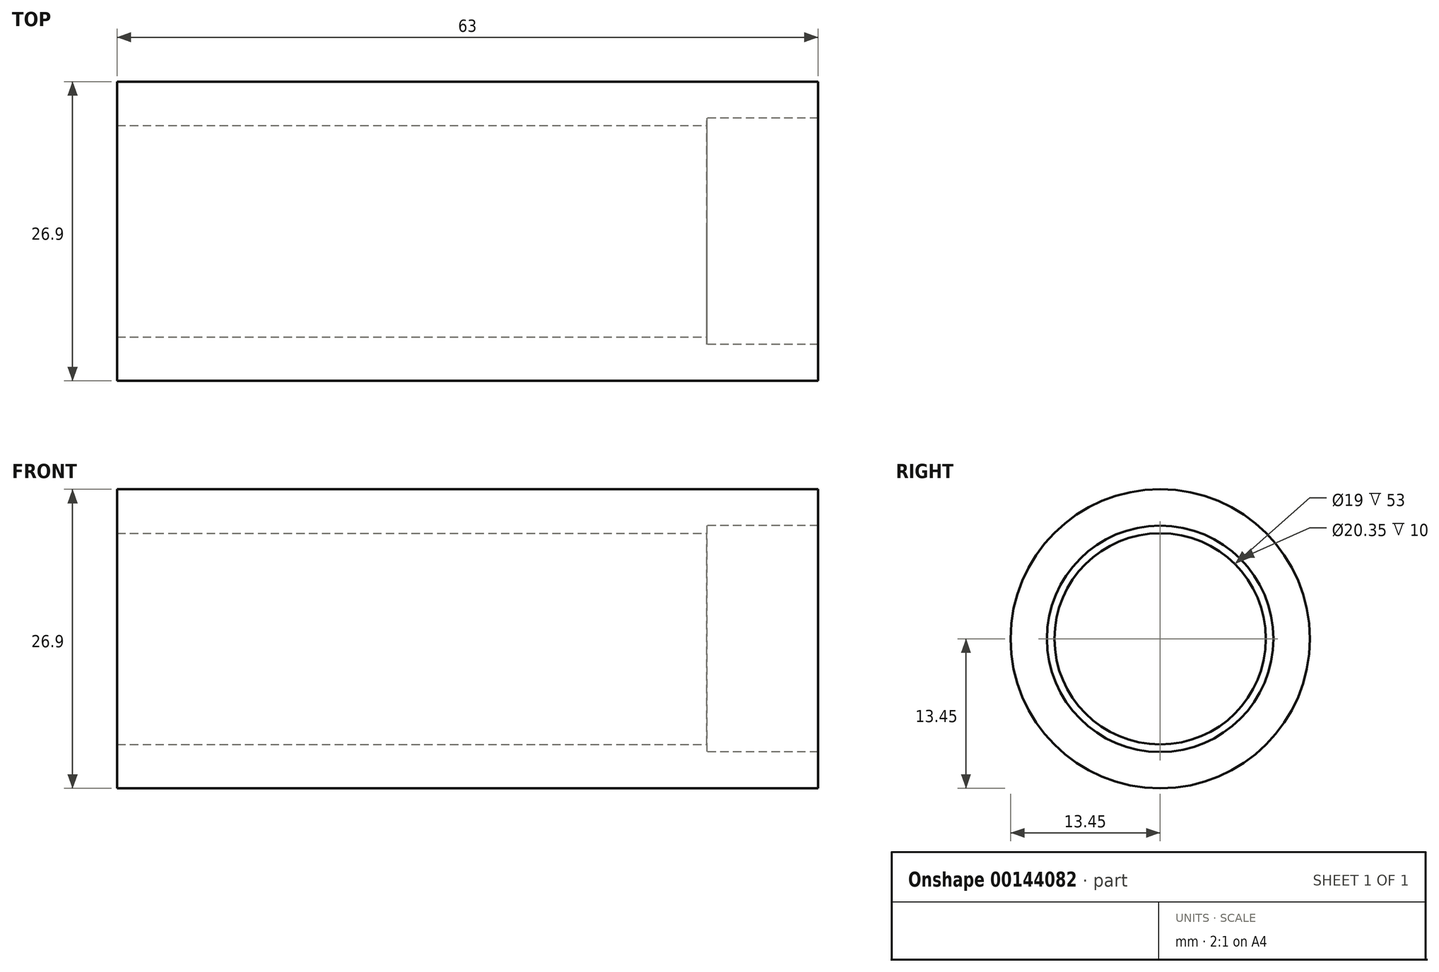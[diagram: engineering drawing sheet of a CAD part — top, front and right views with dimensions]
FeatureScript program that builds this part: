
annotation { "Feature Type Name" : "Feature", "Feature Type Description" : "" }
export const myFeature = defineFeature(function(context is Context, id is Id, definition is map)
    precondition{}
    {
        {
            var Q0;
            Q0=qCreatedBy(makeId("Right.planeOp"),FACE);
            var sketch = newSketch(context, id + "F0", { "sketchPlane" : qUnion([Q0])});
            skCircle(sketch, "E0", {"center": v(0, 0) * mm, "radius": 13.45 * mm});
            skCircle(sketch, "E1", {"center": v(0, 0) * mm, "radius": 9.5 * mm});
            skSolve(sketch);
        }
        {
            var Q0;
            Q0 = qSketchRegion(id + "F0", true);
            extrude(context, id + "F1", {"entities" : qUnion([Q0]), "oppositeDirection" : true, "depth" : 63 * mm});
        }
        {
            var Q0;
            Q0=qCreatedBy(makeId("Front.planeOp"),FACE);
            var sketch = newSketch(context, id + "F2", { "sketchPlane" : qUnion([Q0])});
            skLineSegment(sketch, "E2.0", {"start": v(-63, 13.45) * mm, "end": v(-63, -13.45) * mm, "construction": true});
            skLineSegment(sketch, "E3", {"start": v(-63, 13.45) * mm, "end": v(0, 13.45) * mm, "construction": true});
            skLineSegment(sketch, "E4.0", {"start": v(0, 13.45) * mm, "end": v(0, -13.45) * mm, "construction": true});
            skLineSegment(sketch, "E5", {"start": v(0, 9.38) * mm, "end": v(0, 10.18) * mm});
            skLineSegment(sketch, "E6", {"start": v(0, 10.18) * mm, "end": v(-10, 10.18) * mm});
            skLineSegment(sketch, "E7", {"start": v(-10, 10.18) * mm, "end": v(-10, 9.38) * mm});
            skLineSegment(sketch, "E8", {"start": v(-10, 9.38) * mm, "end": v(0, 9.38) * mm});
            skLineSegment(sketch, "E9", {"start": v(0.87, 9.38) * mm, "end": v(-67.94, 9.38) * mm, "construction": true});
            skSolve(sketch);
        }
        {
            var Q0;
            Q0 = qSketchRegion(id + "F2", true);
            var Q1;
            Q1=makeQuery(id+"F1.opExtrude","SWEPT_FACE",FACE,{"disambiguationData":[OSD([sQuery(id+"F0.wireOp",EDGE,"E1")])]});
            revolve(context, id + "F3", {"operationType" : NewBodyOperationType.REMOVE, "entities" : qUnion([Q0]), "axis" : qUnion([Q1]), "revolveType" : RevolveType.FULL, "oppositeDirection" : true});
        }
    });
